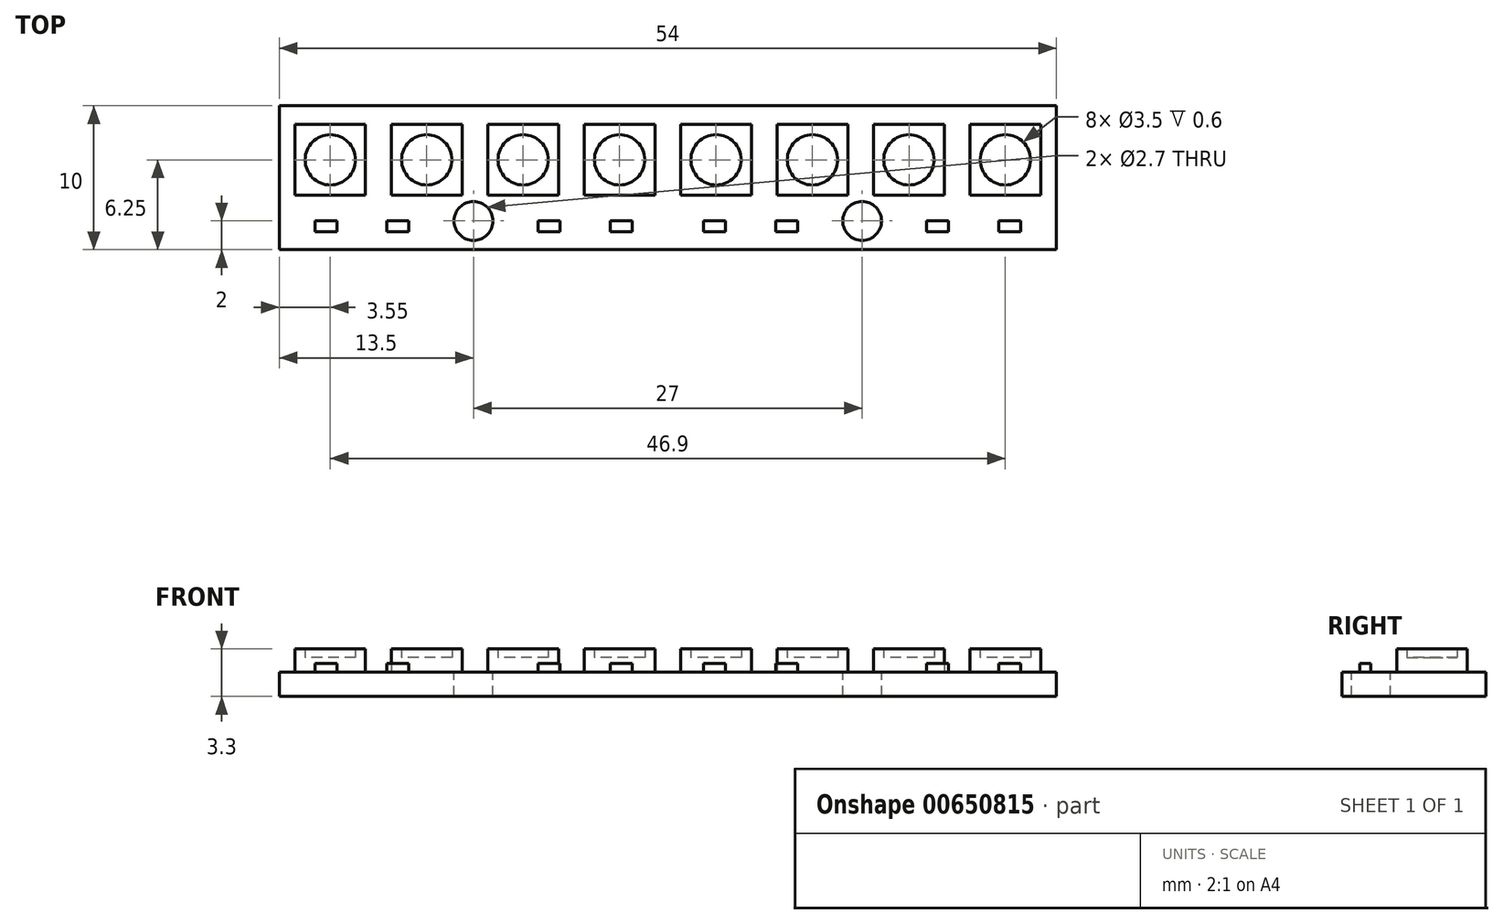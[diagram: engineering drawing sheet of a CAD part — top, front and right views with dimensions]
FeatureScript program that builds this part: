
annotation { "Feature Type Name" : "Feature", "Feature Type Description" : "" }
export const myFeature = defineFeature(function(context is Context, id is Id, definition is map)
    precondition{}
    {
        {
            var Q0;
            Q0=qCreatedBy(makeId("Top.planeOp"),FACE);
            var sketch = newSketch(context, id + "F0", { "sketchPlane" : qUnion([Q0])});
            skLineSegment(sketch, "E0.bottom", {"start": v(27, 0) * mm, "end": v(-27, 0) * mm});
            skLineSegment(sketch, "E0.top", {"start": v(27, 10) * mm, "end": v(-27, 10) * mm});
            skLineSegment(sketch, "E0.left", {"start": v(27, 0) * mm, "end": v(27, 10) * mm});
            skLineSegment(sketch, "E0.right", {"start": v(-27, 0) * mm, "end": v(-27, 10) * mm});
            skPoint(sketch, "E0.middle", {"position": v(0, 5) * mm});
            skLineSegment(sketch, "E1", {"start": v(-13.5, 2) * mm, "end": v(13.5, 2) * mm, "construction": true});
            skPoint(sketch, "E2", {"position": v(0, 2) * mm});
            skCircle(sketch, "E3", {"center": v(13.5, 2) * mm, "radius": 1.35 * mm});
            skCircle(sketch, "E4", {"center": v(-13.5, 2) * mm, "radius": 1.35 * mm});
            skSolve(sketch);
        }
        {
            var Q0;
            Q0=qCreatedBy(makeId("Top.planeOp"),FACE);
            var sketch = newSketch(context, id + "F1", { "sketchPlane" : qUnion([Q0])});
            skLineSegment(sketch, "E5.bottom", {"start": v(-22.99, 2) * mm, "end": v(-24.51, 2) * mm});
            skLineSegment(sketch, "E5.top", {"start": v(-22.99, 1.24) * mm, "end": v(-24.51, 1.24) * mm});
            skLineSegment(sketch, "E5.left", {"start": v(-22.99, 2) * mm, "end": v(-22.99, 1.24) * mm});
            skLineSegment(sketch, "E5.right", {"start": v(-24.51, 2) * mm, "end": v(-24.51, 1.24) * mm});
            skPoint(sketch, "E5.middle", {"position": v(-23.75, 1.62) * mm});
            skLineSegment(sketch, "E6.bottom", {"start": v(-17.99, 2) * mm, "end": v(-19.51, 2) * mm});
            skLineSegment(sketch, "E6.top", {"start": v(-17.99, 1.24) * mm, "end": v(-19.51, 1.24) * mm});
            skLineSegment(sketch, "E6.left", {"start": v(-17.99, 2) * mm, "end": v(-17.99, 1.24) * mm});
            skLineSegment(sketch, "E6.right", {"start": v(-19.51, 2) * mm, "end": v(-19.51, 1.24) * mm});
            skPoint(sketch, "E6.middle", {"position": v(-18.75, 1.62) * mm});
            skLineSegment(sketch, "E7.bottom", {"start": v(-7.49, 2) * mm, "end": v(-9.01, 2) * mm});
            skLineSegment(sketch, "E7.top", {"start": v(-7.49, 1.24) * mm, "end": v(-9.01, 1.24) * mm});
            skLineSegment(sketch, "E7.left", {"start": v(-7.49, 2) * mm, "end": v(-7.49, 1.24) * mm});
            skLineSegment(sketch, "E7.right", {"start": v(-9.01, 2) * mm, "end": v(-9.01, 1.24) * mm});
            skPoint(sketch, "E7.middle", {"position": v(-8.25, 1.62) * mm});
            skLineSegment(sketch, "E8.bottom", {"start": v(-2.49, 2) * mm, "end": v(-4.01, 2) * mm});
            skLineSegment(sketch, "E8.top", {"start": v(-2.49, 1.24) * mm, "end": v(-4.01, 1.24) * mm});
            skLineSegment(sketch, "E8.left", {"start": v(-2.49, 2) * mm, "end": v(-2.49, 1.24) * mm});
            skLineSegment(sketch, "E8.right", {"start": v(-4.01, 2) * mm, "end": v(-4.01, 1.24) * mm});
            skPoint(sketch, "E8.middle", {"position": v(-3.25, 1.62) * mm});
            skLineSegment(sketch, "E9", {"start": v(-3.25, 1.62) * mm, "end": v(-8.25, 1.62) * mm, "construction": true});
            skLineSegment(sketch, "E10", {"start": v(-18.75, 1.62) * mm, "end": v(-23.75, 1.62) * mm, "construction": true});
            skLineSegment(sketch, "E11", {"start": v(-18.75, 1.62) * mm, "end": v(-8.25, 1.62) * mm, "construction": true});
            skPoint(sketch, "E12", {"position": v(-13.5, 1.62) * mm});
            skLineSegment(sketch, "E13.bottom", {"start": v(-21, 8.7) * mm, "end": v(-25.9, 8.7) * mm});
            skLineSegment(sketch, "E13.top", {"start": v(-21, 3.8) * mm, "end": v(-25.9, 3.8) * mm});
            skLineSegment(sketch, "E13.left", {"start": v(-21, 8.7) * mm, "end": v(-21, 3.8) * mm});
            skLineSegment(sketch, "E13.right", {"start": v(-25.9, 8.7) * mm, "end": v(-25.9, 3.8) * mm});
            skPoint(sketch, "E13.middle", {"position": v(-23.45, 6.25) * mm});
            skCircle(sketch, "E14", {"center": v(-23.45, 6.25) * mm, "radius": 1.75 * mm});
            skLineSegment(sketch, "E15.1.0.0", {"start": v(-14.3, 8.7) * mm, "end": v(-14.3, 3.8) * mm});
            skLineSegment(sketch, "E15.1.0.1", {"start": v(-14.3, 8.7) * mm, "end": v(-19.2, 8.7) * mm});
            skLineSegment(sketch, "E15.1.0.2", {"start": v(-19.2, 8.7) * mm, "end": v(-19.2, 3.8) * mm});
            skLineSegment(sketch, "E15.1.0.3", {"start": v(-14.3, 3.8) * mm, "end": v(-19.2, 3.8) * mm});
            skCircle(sketch, "E15.1.0.4", {"center": v(-16.75, 6.25) * mm, "radius": 1.75 * mm});
            skLineSegment(sketch, "E15.2.0.0", {"start": v(-7.6, 8.7) * mm, "end": v(-7.6, 3.8) * mm});
            skLineSegment(sketch, "E15.2.0.1", {"start": v(-7.6, 8.7) * mm, "end": v(-12.5, 8.7) * mm});
            skLineSegment(sketch, "E15.2.0.2", {"start": v(-12.5, 8.7) * mm, "end": v(-12.5, 3.8) * mm});
            skLineSegment(sketch, "E15.2.0.3", {"start": v(-7.6, 3.8) * mm, "end": v(-12.5, 3.8) * mm});
            skCircle(sketch, "E15.2.0.4", {"center": v(-10.05, 6.25) * mm, "radius": 1.75 * mm});
            skLineSegment(sketch, "E15.3.0.0", {"start": v(-0.9, 8.7) * mm, "end": v(-0.9, 3.8) * mm});
            skLineSegment(sketch, "E15.3.0.1", {"start": v(-0.9, 8.7) * mm, "end": v(-5.8, 8.7) * mm});
            skLineSegment(sketch, "E15.3.0.2", {"start": v(-5.8, 8.7) * mm, "end": v(-5.8, 3.8) * mm});
            skLineSegment(sketch, "E15.3.0.3", {"start": v(-0.9, 3.8) * mm, "end": v(-5.8, 3.8) * mm});
            skCircle(sketch, "E15.3.0.4", {"center": v(-3.35, 6.25) * mm, "radius": 1.75 * mm});
            skLineSegment(sketch, "E15.4.0.0", {"start": v(5.8, 8.7) * mm, "end": v(5.8, 3.8) * mm});
            skLineSegment(sketch, "E15.4.0.1", {"start": v(5.8, 8.7) * mm, "end": v(0.9, 8.7) * mm});
            skLineSegment(sketch, "E15.4.0.2", {"start": v(0.9, 8.7) * mm, "end": v(0.9, 3.8) * mm});
            skLineSegment(sketch, "E15.4.0.3", {"start": v(5.8, 3.8) * mm, "end": v(0.9, 3.8) * mm});
            skCircle(sketch, "E15.4.0.4", {"center": v(3.35, 6.25) * mm, "radius": 1.75 * mm});
            skLineSegment(sketch, "E15.5.0.0", {"start": v(12.5, 8.7) * mm, "end": v(12.5, 3.8) * mm});
            skLineSegment(sketch, "E15.5.0.1", {"start": v(12.5, 8.7) * mm, "end": v(7.6, 8.7) * mm});
            skLineSegment(sketch, "E15.5.0.2", {"start": v(7.6, 8.7) * mm, "end": v(7.6, 3.8) * mm});
            skLineSegment(sketch, "E15.5.0.3", {"start": v(12.5, 3.8) * mm, "end": v(7.6, 3.8) * mm});
            skCircle(sketch, "E15.5.0.4", {"center": v(10.05, 6.25) * mm, "radius": 1.75 * mm});
            skLineSegment(sketch, "E15.6.0.0", {"start": v(19.2, 8.7) * mm, "end": v(19.2, 3.8) * mm});
            skLineSegment(sketch, "E15.6.0.1", {"start": v(19.2, 8.7) * mm, "end": v(14.3, 8.7) * mm});
            skLineSegment(sketch, "E15.6.0.2", {"start": v(14.3, 8.7) * mm, "end": v(14.3, 3.8) * mm});
            skLineSegment(sketch, "E15.6.0.3", {"start": v(19.2, 3.8) * mm, "end": v(14.3, 3.8) * mm});
            skCircle(sketch, "E15.6.0.4", {"center": v(16.75, 6.25) * mm, "radius": 1.75 * mm});
            skLineSegment(sketch, "E15.7.0.0", {"start": v(25.9, 8.7) * mm, "end": v(25.9, 3.8) * mm});
            skLineSegment(sketch, "E15.7.0.1", {"start": v(25.9, 8.7) * mm, "end": v(21, 8.7) * mm});
            skLineSegment(sketch, "E15.7.0.2", {"start": v(21, 8.7) * mm, "end": v(21, 3.8) * mm});
            skLineSegment(sketch, "E15.7.0.3", {"start": v(25.9, 3.8) * mm, "end": v(21, 3.8) * mm});
            skCircle(sketch, "E15.7.0.4", {"center": v(23.45, 6.25) * mm, "radius": 1.75 * mm});
            skLineSegment(sketch, "E15.direction1", {"start": v(-21, 3.8) * mm, "end": v(-14.3, 3.8) * mm, "construction": true});
            skLineSegment(sketch, "E16", {"start": v(-0.9, 3.8) * mm, "end": v(0.9, 3.8) * mm, "construction": true});
            skPoint(sketch, "E17", {"position": v(0, 3.8) * mm});
            skLineSegment(sketch, "E18.MirrorCS", {"start": v(2.49, 2) * mm, "end": v(2.49, 1.24) * mm});
            skLineSegment(sketch, "E19.MirrorCS", {"start": v(2.49, 2) * mm, "end": v(4.01, 2) * mm});
            skLineSegment(sketch, "E20.MirrorCS", {"start": v(4.01, 2) * mm, "end": v(4.01, 1.24) * mm});
            skLineSegment(sketch, "E21.MirrorCS", {"start": v(2.49, 1.24) * mm, "end": v(4.01, 1.24) * mm});
            skLineSegment(sketch, "E22.MirrorCS", {"start": v(7.49, 2) * mm, "end": v(7.49, 1.24) * mm});
            skLineSegment(sketch, "E23.MirrorCS", {"start": v(7.49, 1.24) * mm, "end": v(9.01, 1.24) * mm});
            skLineSegment(sketch, "E24.MirrorCS", {"start": v(7.49, 2) * mm, "end": v(9.01, 2) * mm});
            skLineSegment(sketch, "E25.MirrorCS", {"start": v(9.01, 2) * mm, "end": v(9.01, 1.24) * mm});
            skLineSegment(sketch, "E26.MirrorCS", {"start": v(17.99, 2) * mm, "end": v(17.99, 1.24) * mm});
            skLineSegment(sketch, "E27.MirrorCS", {"start": v(17.99, 1.24) * mm, "end": v(19.51, 1.24) * mm});
            skLineSegment(sketch, "E28.MirrorCS", {"start": v(19.51, 2) * mm, "end": v(19.51, 1.24) * mm});
            skLineSegment(sketch, "E29.MirrorCS", {"start": v(22.99, 2) * mm, "end": v(22.99, 1.24) * mm});
            skLineSegment(sketch, "E30.MirrorCS", {"start": v(22.99, 2) * mm, "end": v(24.51, 2) * mm});
            skLineSegment(sketch, "E31.MirrorCS", {"start": v(24.51, 2) * mm, "end": v(24.51, 1.24) * mm});
            skLineSegment(sketch, "E32.MirrorCS", {"start": v(22.99, 1.24) * mm, "end": v(24.51, 1.24) * mm});
            skLineSegment(sketch, "E33.MirrorCS", {"start": v(17.99, 2) * mm, "end": v(19.51, 2) * mm});
            skSolve(sketch);
        }
        {
            var Q0;
            Q0=makeQuery(id+"F0.imprint","IMPRINT",FACE,{"disambiguationData":[TD([[makeQuery(id+"F0.imprint","IMPRINT",EDGE,{"derivedFrom":sQuery(id+"F0.wireOp",EDGE,"E0.bottom")}),-1.0]])]});
            extrude(context, id + "F2", {"entities" : qUnion([Q0]), "oppositeDirection" : true, "depth" : 1.7 * mm, "offsetDistance" : 25 * mm});
        }
        {
            var Q0;
            Q0=makeQuery(id+"F1.imprint","IMPRINT",FACE,{"disambiguationData":[TD([[makeQuery(id+"F1.imprint","IMPRINT",EDGE,{"derivedFrom":sQuery(id+"F1.wireOp",EDGE,"E13.bottom")}),1.0]])]});
            var Q1;
            Q1=makeQuery(id+"F1.imprint","IMPRINT",FACE,{"disambiguationData":[TD([[makeQuery(id+"F1.imprint","IMPRINT",EDGE,{"derivedFrom":sQuery(id+"F1.wireOp",EDGE,"E15.1.0.0")}),-1.0]])]});
            var Q2;
            Q2=makeQuery(id+"F1.imprint","IMPRINT",FACE,{"disambiguationData":[TD([[makeQuery(id+"F1.imprint","IMPRINT",EDGE,{"derivedFrom":sQuery(id+"F1.wireOp",EDGE,"E15.2.0.0")}),-1.0]])]});
            var Q3;
            Q3=makeQuery(id+"F1.imprint","IMPRINT",FACE,{"disambiguationData":[TD([[makeQuery(id+"F1.imprint","IMPRINT",EDGE,{"derivedFrom":sQuery(id+"F1.wireOp",EDGE,"E15.3.0.0")}),-1.0]])]});
            var Q4;
            Q4=makeQuery(id+"F1.imprint","IMPRINT",FACE,{"disambiguationData":[TD([[makeQuery(id+"F1.imprint","IMPRINT",EDGE,{"derivedFrom":sQuery(id+"F1.wireOp",EDGE,"E15.4.0.0")}),-1.0]])]});
            var Q5;
            Q5=makeQuery(id+"F1.imprint","IMPRINT",FACE,{"disambiguationData":[TD([[makeQuery(id+"F1.imprint","IMPRINT",EDGE,{"derivedFrom":sQuery(id+"F1.wireOp",EDGE,"E15.5.0.0")}),-1.0]])]});
            var Q6;
            Q6=makeQuery(id+"F1.imprint","IMPRINT",FACE,{"disambiguationData":[TD([[makeQuery(id+"F1.imprint","IMPRINT",EDGE,{"derivedFrom":sQuery(id+"F1.wireOp",EDGE,"E15.6.0.0")}),-1.0]])]});
            var Q7;
            Q7=makeQuery(id+"F1.imprint","IMPRINT",FACE,{"disambiguationData":[TD([[makeQuery(id+"F1.imprint","IMPRINT",EDGE,{"derivedFrom":sQuery(id+"F1.wireOp",EDGE,"E15.7.0.0")}),-1.0]])]});
            extrude(context, id + "F3", {"entities" : qUnion([Q0, Q1, Q2, Q3, Q4, Q5, Q6, Q7]), "depth" : 1.6 * mm, "offsetDistance" : 25 * mm});
        }
        {
            var Q0;
            Q0=makeQuery(id+"F1.imprint","IMPRINT",FACE,{"disambiguationData":[TD([[makeQuery(id+"F1.imprint","IMPRINT",EDGE,{"derivedFrom":sQuery(id+"F1.wireOp",EDGE,"E15.7.0.4")}),1.0]])]});
            var Q1;
            Q1=makeQuery(id+"F1.imprint","IMPRINT",FACE,{"disambiguationData":[TD([[makeQuery(id+"F1.imprint","IMPRINT",EDGE,{"derivedFrom":sQuery(id+"F1.wireOp",EDGE,"E15.6.0.4")}),1.0]])]});
            var Q2;
            Q2=makeQuery(id+"F1.imprint","IMPRINT",FACE,{"disambiguationData":[TD([[makeQuery(id+"F1.imprint","IMPRINT",EDGE,{"derivedFrom":sQuery(id+"F1.wireOp",EDGE,"E15.5.0.4")}),1.0]])]});
            var Q3;
            Q3=makeQuery(id+"F1.imprint","IMPRINT",FACE,{"disambiguationData":[TD([[makeQuery(id+"F1.imprint","IMPRINT",EDGE,{"derivedFrom":sQuery(id+"F1.wireOp",EDGE,"E15.4.0.4")}),1.0]])]});
            var Q4;
            Q4=makeQuery(id+"F1.imprint","IMPRINT",FACE,{"disambiguationData":[TD([[makeQuery(id+"F1.imprint","IMPRINT",EDGE,{"derivedFrom":sQuery(id+"F1.wireOp",EDGE,"E15.3.0.4")}),1.0]])]});
            var Q5;
            Q5=makeQuery(id+"F1.imprint","IMPRINT",FACE,{"disambiguationData":[TD([[makeQuery(id+"F1.imprint","IMPRINT",EDGE,{"derivedFrom":sQuery(id+"F1.wireOp",EDGE,"E15.2.0.4")}),1.0]])]});
            var Q6;
            Q6=makeQuery(id+"F1.imprint","IMPRINT",FACE,{"disambiguationData":[TD([[makeQuery(id+"F1.imprint","IMPRINT",EDGE,{"derivedFrom":sQuery(id+"F1.wireOp",EDGE,"E15.1.0.4")}),1.0]])]});
            var Q7;
            Q7=makeQuery(id+"F1.imprint","IMPRINT",FACE,{"disambiguationData":[TD([[makeQuery(id+"F1.imprint","IMPRINT",EDGE,{"derivedFrom":sQuery(id+"F1.wireOp",EDGE,"E14")}),1.0]])]});
            extrude(context, id + "F4", {"entities" : qUnion([Q0, Q1, Q2, Q3, Q4, Q5, Q6, Q7]), "operationType" : NewBodyOperationType.ADD, "depth" : 1 * mm, "offsetDistance" : 25 * mm});
        }
        {
            var Q0;
            Q0=makeQuery(id+"F1.imprint","IMPRINT",FACE,{"disambiguationData":[TD([[makeQuery(id+"F1.imprint","IMPRINT",EDGE,{"derivedFrom":sQuery(id+"F1.wireOp",EDGE,"E29.MirrorCS")}),1.0]])]});
            var Q1;
            Q1=makeQuery(id+"F1.imprint","IMPRINT",FACE,{"disambiguationData":[TD([[makeQuery(id+"F1.imprint","IMPRINT",EDGE,{"derivedFrom":sQuery(id+"F1.wireOp",EDGE,"E26.MirrorCS")}),1.0]])]});
            var Q2;
            Q2=makeQuery(id+"F1.imprint","IMPRINT",FACE,{"disambiguationData":[TD([[makeQuery(id+"F1.imprint","IMPRINT",EDGE,{"derivedFrom":sQuery(id+"F1.wireOp",EDGE,"E22.MirrorCS")}),1.0]])]});
            var Q3;
            Q3=makeQuery(id+"F1.imprint","IMPRINT",FACE,{"disambiguationData":[TD([[makeQuery(id+"F1.imprint","IMPRINT",EDGE,{"derivedFrom":sQuery(id+"F1.wireOp",EDGE,"E18.MirrorCS")}),1.0]])]});
            var Q4;
            Q4=makeQuery(id+"F1.imprint","IMPRINT",FACE,{"disambiguationData":[TD([[makeQuery(id+"F1.imprint","IMPRINT",EDGE,{"derivedFrom":sQuery(id+"F1.wireOp",EDGE,"E8.bottom")}),1.0]])]});
            var Q5;
            Q5=makeQuery(id+"F1.imprint","IMPRINT",FACE,{"disambiguationData":[TD([[makeQuery(id+"F1.imprint","IMPRINT",EDGE,{"derivedFrom":sQuery(id+"F1.wireOp",EDGE,"E7.bottom")}),1.0]])]});
            var Q6;
            Q6=makeQuery(id+"F1.imprint","IMPRINT",FACE,{"disambiguationData":[TD([[makeQuery(id+"F1.imprint","IMPRINT",EDGE,{"derivedFrom":sQuery(id+"F1.wireOp",EDGE,"E6.bottom")}),1.0]])]});
            var Q7;
            Q7=makeQuery(id+"F1.imprint","IMPRINT",FACE,{"disambiguationData":[TD([[makeQuery(id+"F1.imprint","IMPRINT",EDGE,{"derivedFrom":sQuery(id+"F1.wireOp",EDGE,"E5.bottom")}),1.0]])]});
            extrude(context, id + "F5", {"entities" : qUnion([Q0, Q1, Q2, Q3, Q4, Q5, Q6, Q7]), "depth" : 0.6 * mm, "offsetDistance" : 25 * mm});
        }
    });
